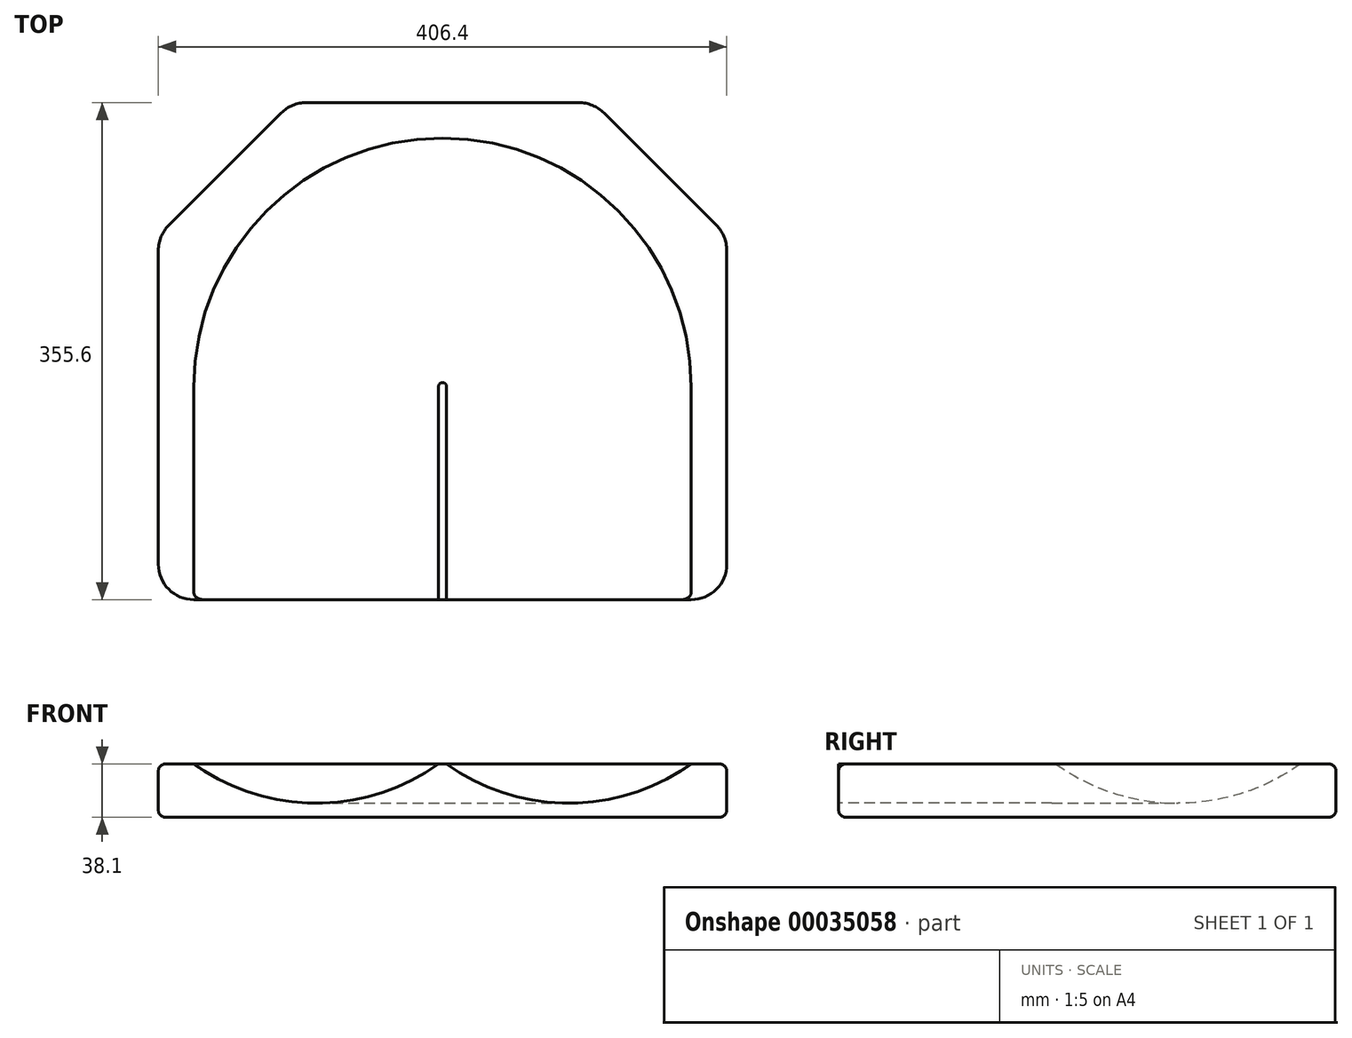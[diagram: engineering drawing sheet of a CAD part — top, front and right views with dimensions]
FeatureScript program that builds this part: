
annotation { "Feature Type Name" : "Feature", "Feature Type Description" : "" }
export const myFeature = defineFeature(function(context is Context, id is Id, definition is map)
    precondition{}
    {
        {
            var Q0;
            Q0=qCreatedBy(makeId("Top.planeOp"),FACE);
            var sketch = newSketch(context, id + "F0", { "sketchPlane" : qUnion([Q0])});
            skLineSegment(sketch, "E0.rect.bottom", {"start": v(-97.43, 177.8) * mm, "end": v(97.43, 177.8) * mm});
            skLineSegment(sketch, "E0.rect.top", {"start": v(-177.8, -177.8) * mm, "end": v(177.8, -177.8) * mm});
            skLineSegment(sketch, "E0.rect.left", {"start": v(-203.2, 72.03) * mm, "end": v(-203.2, -152.4) * mm});
            skLineSegment(sketch, "E0.rect.right", {"start": v(203.2, 82.55) * mm, "end": v(203.2, -152.4) * mm});
            skPoint(sketch, "E0.rect.middle", {"position": v(0, 0) * mm});
            skPoint(sketch, "E1.visualSharp", {"position": v(-203.2, 177.8) * mm});
            skPoint(sketch, "E2.visualSharp", {"position": v(203.2, 177.8) * mm});
            skPoint(sketch, "E3.visualSharp", {"position": v(-203.2, -177.8) * mm});
            skPoint(sketch, "E4.visualSharp", {"position": v(203.2, -177.8) * mm});
            skLineSegment(sketch, "E5", {"start": v(-115.39, 170.36) * mm, "end": v(-195.76, 89.99) * mm});
            skLineSegment(sketch, "E6", {"start": v(0, 0) * mm, "end": v(0, -177.8) * mm, "construction": true});
            skLineSegment(sketch, "E7.MirrorCS", {"start": v(-285.75, 285.75) * mm, "end": v(-463.55, 285.75) * mm});
            skPoint(sketch, "E8.visualSharp", {"position": v(-203.2, 82.55) * mm});
            skArc(sketch, "E8.filletArc", {"start": v(-195.76, 89.99) * mm, "mid": v(-201.27, 81.75) * mm, "end": v(-203.2, 72.03) * mm});
            skPoint(sketch, "E9.visualSharp", {"position": v(-107.95, 177.8) * mm});
            skArc(sketch, "E9.filletArc", {"start": v(-97.43, 177.8) * mm, "mid": v(-107.15, 175.87) * mm, "end": v(-115.39, 170.36) * mm});
            skLineSegment(sketch, "E10.MirrorCS", {"start": v(115.39, 170.36) * mm, "end": v(195.76, 89.99) * mm});
            skArc(sketch, "E11.MirrorCS", {"start": v(97.43, 177.8) * mm, "mid": v(107.15, 175.87) * mm, "end": v(115.39, 170.36) * mm});
            skPoint(sketch, "E12.MirrorP", {"position": v(203.2, 82.55) * mm});
            skArc(sketch, "E13.MirrorCS", {"start": v(195.76, 89.99) * mm, "mid": v(201.27, 81.75) * mm, "end": v(203.2, 72.03) * mm});
            skArc(sketch, "E14", {"start": v(-203.2, -152.4) * mm, "mid": v(-195.76, -170.36) * mm, "end": v(-177.8, -177.8) * mm});
            skArc(sketch, "E15", {"start": v(177.8, -177.8) * mm, "mid": v(195.76, -170.36) * mm, "end": v(203.2, -152.4) * mm});
            skSolve(sketch);
        }
        {
            var Q0;
            Q0=makeQuery(id+"F0.imprint","IMPRINT",FACE,{"disambiguationData":[TD([[makeQuery(id+"F0.imprint","IMPRINT",EDGE,{"derivedFrom":sQuery(id+"F0.wireOp",EDGE,"E0.rect.bottom")}),-1.0]])]});
            extrude(context, id + "F1", {"entities" : qUnion([Q0]), "depth" : 38.1 * mm});
        }
        {
            var Q0;
            Q0=makeQuery(id+"F1.opExtrude","CAP_FACE",FACE,{"disambiguationData":[OSD([sQuery(id+"F0.wireOp",EDGE,"E0.rect.bottom"),sQuery(id+"F0.wireOp",EDGE,"E0.rect.top"),sQuery(id+"F0.wireOp",EDGE,"E0.rect.left"),sQuery(id+"F0.wireOp",EDGE,"E0.rect.right"),sQuery(id+"F0.wireOp",EDGE,"E1.filletArc"),sQuery(id+"F0.wireOp",EDGE,"E2.filletArc"),sQuery(id+"F0.wireOp",EDGE,"E3.filletArc"),sQuery(id+"F0.wireOp",EDGE,"E4.filletArc")])],"isStart":false});
            var sketch = newSketch(context, id + "F2", { "sketchPlane" : qUnion([Q0])});
            skLineSegment(sketch, "E16", {"start": v(0, 0) * mm, "end": v(0, -177.8) * mm, "construction": true});
            skLineSegment(sketch, "E17", {"start": v(-130.84, -177.8) * mm, "end": v(-130.84, -25.4) * mm});
            skLineSegment(sketch, "E18.MirrorCS", {"start": v(130.84, -206.44) * mm, "end": v(130.84, -25.4) * mm});
            skPoint(sketch, "E19.orphan", {"position": v(-130.84, -177.8) * mm});
            skPoint(sketch, "E20.orphan", {"position": v(130.84, -177.8) * mm});
            skArc(sketch, "E21", {"start": v(130.84, -25.4) * mm, "mid": v(0, 105.44) * mm, "end": v(-130.84, -25.4) * mm});
            skSolve(sketch);
        }
        {
            var Q0;
            Q0=makeQuery(id+"F1.opExtrude","SWEPT_FACE",FACE,{"disambiguationData":[OSD([sQuery(id+"F0.wireOp",EDGE,"E0.rect.top")])]});
            var sketch = newSketch(context, id + "F3", { "sketchPlane" : qUnion([Q0])});
            skLineSegment(sketch, "E22", {"start": v(-177.8, 38.1) * mm, "end": v(-95.21, 38.1) * mm, "construction": true});
            skArc(sketch, "E23", {"start": v(-177.8, 38.1) * mm, "mid": v(-90.35, 10) * mm, "end": v(-2.9, 38.1) * mm});
            skPoint(sketch, "E24.endSnap0", {"position": v(0, 38.1) * mm});
            skSolve(sketch);
        }
        {
            var Q0;
            {var subQ2=sQuery(id+"F3.wireOp",EDGE,"E23");Q0=makeQuery(id+"F3.imprint","IMPRINT",FACE,{"disambiguationData":[TD([[makeQuery(id+"F3.imprint","IMPRINT",EDGE,{"derivedFrom":subQ2}),1.0]])]});}
            var Q1;
            Q1=sQuery(id+"F2.wireOp",EDGE,"E17");
            var Q2;
            Q2=sQuery(id+"F2.wireOp",EDGE,"E21");
            var Q3;
            Q3=sQuery(id+"F2.wireOp",EDGE,"E18.MirrorCS");
            sweep(context, id + "F4", {"operationType" : NewBodyOperationType.REMOVE, "profiles" : qUnion([Q0]), "path" : qUnion([Q1, Q2, Q3])});
        }
        {
            var Q0;
            Q0=makeQuery(id+"F1.opExtrude","CAP_EDGE",EDGE,{"disambiguationData":[OSD([sQuery(id+"F0.wireOp",EDGE,"E14")])],"isStart":false});
            var Q1;
            Q1=makeQuery(id+"F1.opExtrude","CAP_EDGE",EDGE,{"disambiguationData":[OSD([sQuery(id+"F0.wireOp",EDGE,"E0.rect.left")])],"isStart":false});
            var Q2;
            Q2=makeQuery(id+"F1.opExtrude","CAP_EDGE",EDGE,{"disambiguationData":[OSD([sQuery(id+"F0.wireOp",EDGE,"E5")])],"isStart":false});
            var Q3;
            Q3=makeQuery(id+"F1.opExtrude","CAP_EDGE",EDGE,{"disambiguationData":[OSD([sQuery(id+"F0.wireOp",EDGE,"E8.filletArc")])],"isStart":false});
            var Q4;
            Q4=makeQuery(id+"F1.opExtrude","CAP_EDGE",EDGE,{"disambiguationData":[OSD([sQuery(id+"F0.wireOp",EDGE,"E9.filletArc")])],"isStart":false});
            fillet(context, id + "F5", {"entities" : qUnion([Q0, Q1, Q2, Q3, Q4]), "radius" : 5.08 * mm, "tangentPropagation" : true, "allowEdgeOverflow" : false});
        }
        {
            var Q0;
            Q0=makeQuery(id+"F1.opExtrude","CAP_FACE",FACE,{"disambiguationData":[OSD([sQuery(id+"F0.wireOp",EDGE,"E0.rect.bottom"),sQuery(id+"F0.wireOp",EDGE,"E0.rect.top"),sQuery(id+"F0.wireOp",EDGE,"E0.rect.left"),sQuery(id+"F0.wireOp",EDGE,"E0.rect.right"),sQuery(id+"F0.wireOp",EDGE,"E5"),sQuery(id+"F0.wireOp",EDGE,"E8.filletArc"),sQuery(id+"F0.wireOp",EDGE,"E9.filletArc"),sQuery(id+"F0.wireOp",EDGE,"E10.MirrorCS"),sQuery(id+"F0.wireOp",EDGE,"E11.MirrorCS"),sQuery(id+"F0.wireOp",EDGE,"E13.MirrorCS"),sQuery(id+"F0.wireOp",EDGE,"E14"),sQuery(id+"F0.wireOp",EDGE,"E15")])],"isStart":true});
            fillet(context, id + "F6", {"entities" : qUnion([Q0]), "radius" : 5.08 * mm, "tangentPropagation" : true, "allowEdgeOverflow" : false});
        }
    });
